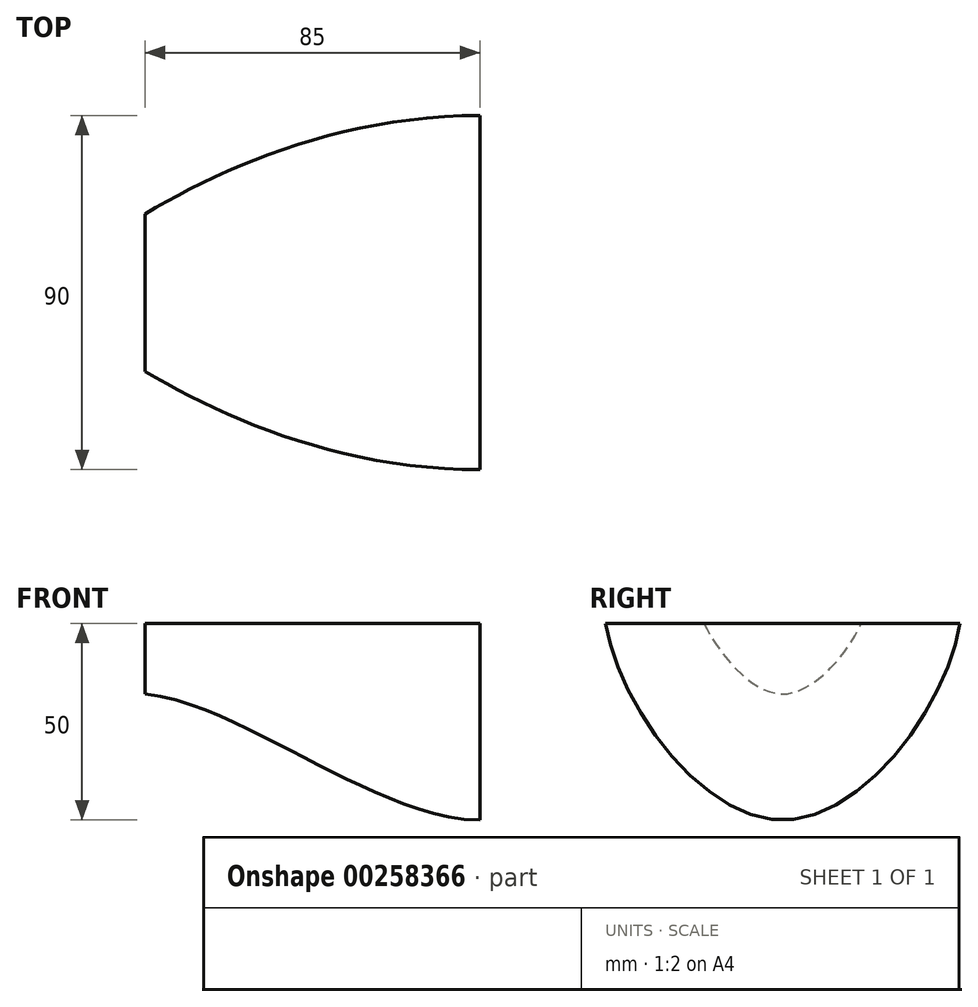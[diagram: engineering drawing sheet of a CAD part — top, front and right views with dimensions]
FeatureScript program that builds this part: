
annotation { "Feature Type Name" : "Feature", "Feature Type Description" : "" }
export const myFeature = defineFeature(function(context is Context, id is Id, definition is map)
    precondition{}
    {
        {
            var Q0;
            Q0=qCreatedBy(makeId("Right.planeOp"),FACE);
            var sketch = newSketch(context, id + "F0", { "sketchPlane" : qUnion([Q0])});
            skFitSpline(sketch, "E0", {"points": [v(-45, 0) * mm, v(0, -50) * mm, v(45, 0) * mm], "startDerivative": vector(18, -120) * mm, "endDerivative": vector(18, 120) * mm});
            skLineSegment(sketch, "E1", {"start": v(-45, 0) * mm, "end": v(45, 0) * mm});
            skSolve(sketch);
        }
        {
            var Q0;
            Q0=qCreatedBy(makeId("Right.planeOp"),FACE);
            cPlane(context, id + "F1", {"entities" : qUnion([Q0]), "cplaneType" : CPlaneType.OFFSET, "offset" : 85 * mm, "oppositeDirection" : true, "width" : 152.4 * mm, "height" : 152.4 * mm});
        }
        {
            var Q0;
            Q0=qCreatedBy(id+"F1.planeOp",FACE);
            var sketch = newSketch(context, id + "F2", { "sketchPlane" : qUnion([Q0])});
            skFitSpline(sketch, "E2", {"points": [v(-20, 0) * mm, v(0, -18) * mm, v(20, 0) * mm], "startDerivative": vector(12, -30) * mm, "endDerivative": vector(12, 30) * mm});
            skLineSegment(sketch, "E3", {"start": v(20, 0) * mm, "end": v(-20, 0) * mm});
            skSolve(sketch);
        }
        {
            var Q0;
            Q0=qCreatedBy(makeId("Front.planeOp"),FACE);
            var sketch = newSketch(context, id + "F3", { "sketchPlane" : qUnion([Q0])});
            skFitSpline(sketch, "E4", {"points": [v(-85, -18) * mm, v(0, -50) * mm], "startDerivative": vector(70.14, -6) * mm, "endDerivative": vector(77.28, 0) * mm});
            skSolve(sketch);
        }
        {
            var Q0;
            Q0=qCreatedBy(makeId("Top.planeOp"),FACE);
            var sketch = newSketch(context, id + "F4", { "sketchPlane" : qUnion([Q0])});
            skFitSpline(sketch, "E5", {"points": [v(-85, 20) * mm, v(0, 45) * mm], "startDerivative": vector(60, 36) * mm, "endDerivative": vector(105, 0) * mm});
            skFitSpline(sketch, "E6", {"points": [v(-85, -20) * mm, v(0, -45) * mm], "startDerivative": vector(60, -36) * mm, "endDerivative": vector(105, 0) * mm});
            skSolve(sketch);
        }
        {
            var Q0;
            Q0=makeQuery(id+"F0.imprint","IMPRINT",FACE,{"disambiguationData":[TD([[makeQuery(id+"F0.imprint","IMPRINT",EDGE,{"derivedFrom":sQuery(id+"F0.wireOp",EDGE,"E0")}),1.0]])]});
            var Q1;
            Q1=makeQuery(id+"F2.imprint","IMPRINT",FACE,{"disambiguationData":[TD([[makeQuery(id+"F2.imprint","IMPRINT",EDGE,{"derivedFrom":sQuery(id+"F2.wireOp",EDGE,"E2")}),1.0]])]});
            var Q2;
            Q2=sQuery(id+"F4.wireOp",EDGE,"E5");
            var Q3;
            Q3=sQuery(id+"F4.wireOp",EDGE,"E6");
            var Q4;
            Q4=sQuery(id+"F3.wireOp",EDGE,"E4");
            loft(context, id + "F5", {"addGuides" : true, "sheetProfilesArray" : [{ "sheetProfileEntities" : qUnion([Q0]) }, { "sheetProfileEntities" : qUnion([Q1]) }], "guidesArray" : [{ "guideEntities" : qUnion([Q2]), "guideDerivativeType" : LoftGuideDerivativeType.DEFAULT, "guideDerivativeMagnitude" : 1 }, { "guideEntities" : qUnion([Q3]), "guideDerivativeType" : LoftGuideDerivativeType.DEFAULT, "guideDerivativeMagnitude" : 1 }, { "guideEntities" : qUnion([Q4]), "guideDerivativeType" : LoftGuideDerivativeType.DEFAULT, "guideDerivativeMagnitude" : 1 }]});
        }
    });
